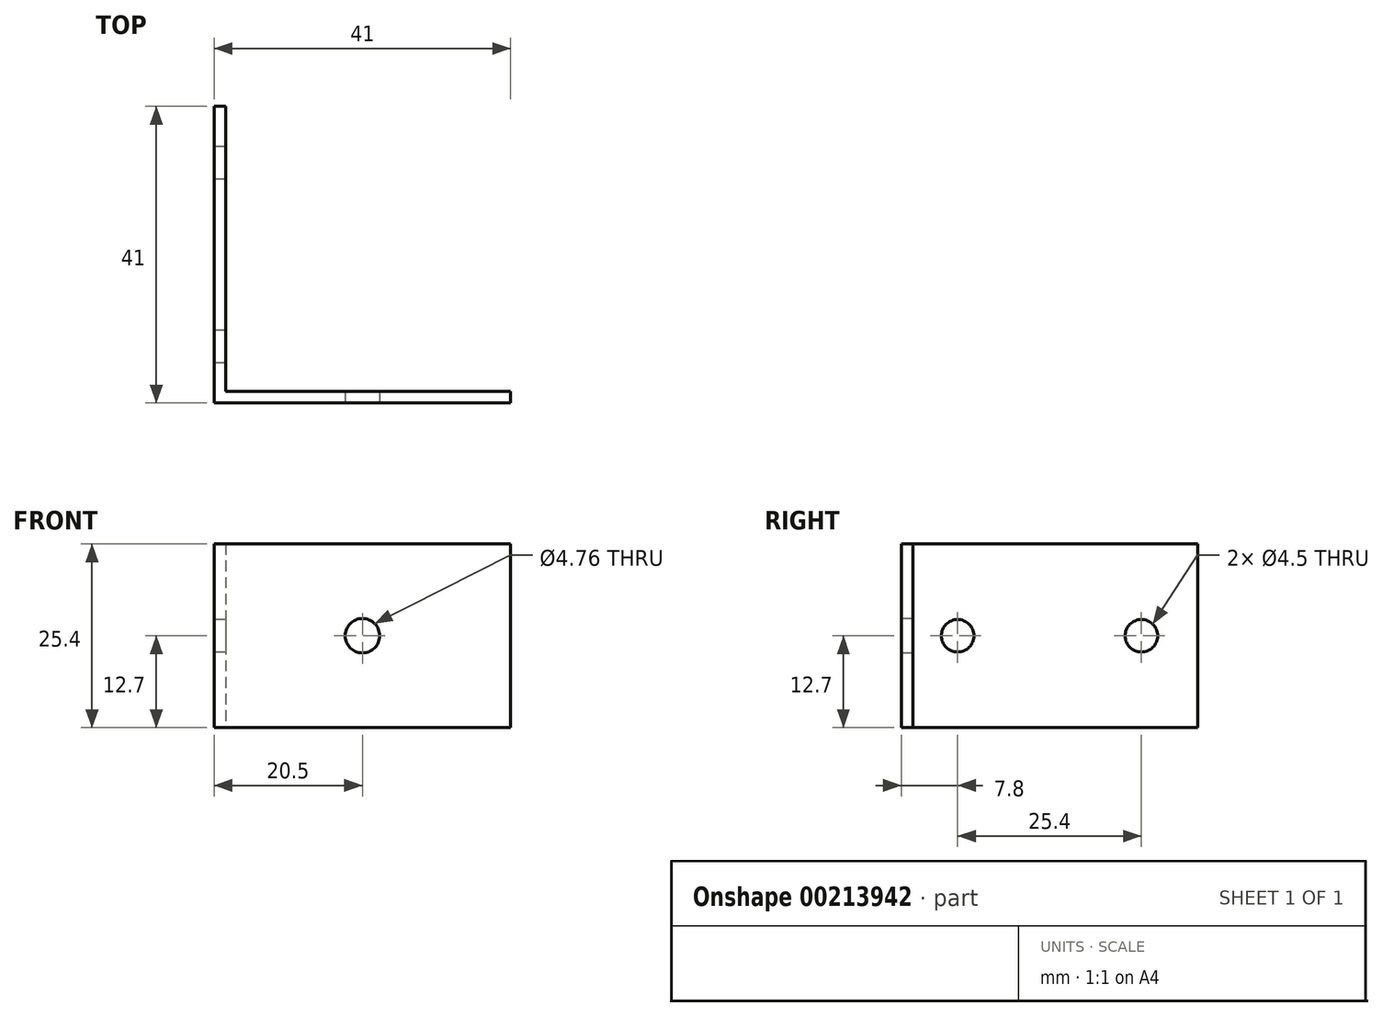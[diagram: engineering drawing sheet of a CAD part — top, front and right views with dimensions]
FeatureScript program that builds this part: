
annotation { "Feature Type Name" : "Feature", "Feature Type Description" : "" }
export const myFeature = defineFeature(function(context is Context, id is Id, definition is map)
    precondition{}
    {
        {
            var Q0;
            Q0=qCreatedBy(makeId("Top.planeOp"),FACE);
            var sketch = newSketch(context, id + "F0", { "sketchPlane" : qUnion([Q0])});
            skLineSegment(sketch, "E0", {"start": v(-30.75, 41) * mm, "end": v(-30.75, 0) * mm});
            skLineSegment(sketch, "E1", {"start": v(-30.75, 0) * mm, "end": v(10.25, 0) * mm});
            skLineSegment(sketch, "E2", {"start": v(10.25, 0) * mm, "end": v(10.25, 1.6) * mm});
            skLineSegment(sketch, "E3", {"start": v(10.25, 1.6) * mm, "end": v(-29.15, 1.6) * mm});
            skLineSegment(sketch, "E4", {"start": v(-29.15, 1.6) * mm, "end": v(-29.15, 41) * mm});
            skLineSegment(sketch, "E5", {"start": v(-29.15, 41) * mm, "end": v(-30.75, 41) * mm});
            skSolve(sketch);
        }
        {
            var Q0;
            Q0 = qSketchRegion(id + "F0", true);
            extrude(context, id + "F1", {"entities" : qUnion([Q0]), "depth" : 25.4 * mm});
        }
        {
            var Q0;
            Q0=makeQuery(id+"F1.opExtrude","SWEPT_FACE",FACE,{"disambiguationData":[OSD([sQuery(id+"F0.wireOp",EDGE,"E0")])]});
            var sketch = newSketch(context, id + "F2", { "sketchPlane" : qUnion([Q0])});
            skPoint(sketch, "E6", {"position": v(-41, 12.7) * mm});
            skCircle(sketch, "E7", {"center": v(-33.2, 12.7) * mm, "radius": 2.25 * mm});
            skCircle(sketch, "E8", {"center": v(-7.8, 12.7) * mm, "radius": 2.25 * mm});
            skSolve(sketch);
        }
        {
            var Q0;
            Q0 = qSketchRegion(id + "F2", true);
            extrude(context, id + "F3", {"entities" : qUnion([Q0]), "operationType" : NewBodyOperationType.REMOVE, "endBound" : BoundingType.THROUGH_ALL, "oppositeDirection" : true, "depth" : 25 * mm});
        }
        {
            var Q0;
            Q0=makeQuery(id+"F1.opExtrude","SWEPT_FACE",FACE,{"disambiguationData":[OSD([sQuery(id+"F0.wireOp",EDGE,"E1")])]});
            var sketch = newSketch(context, id + "F4", { "sketchPlane" : qUnion([Q0])});
            skPoint(sketch, "E9", {"position": v(10.25, 12.7) * mm});
            skPoint(sketch, "E10", {"position": v(-10.25, 25.4) * mm});
            skCircle(sketch, "E11", {"center": v(-10.25, 12.7) * mm, "radius": 2.38 * mm});
            skSolve(sketch);
        }
        {
            var Q0;
            Q0 = qSketchRegion(id + "F4", true);
            extrude(context, id + "F5", {"entities" : qUnion([Q0]), "operationType" : NewBodyOperationType.REMOVE, "endBound" : BoundingType.THROUGH_ALL, "oppositeDirection" : true, "depth" : 25 * mm});
        }
    });
